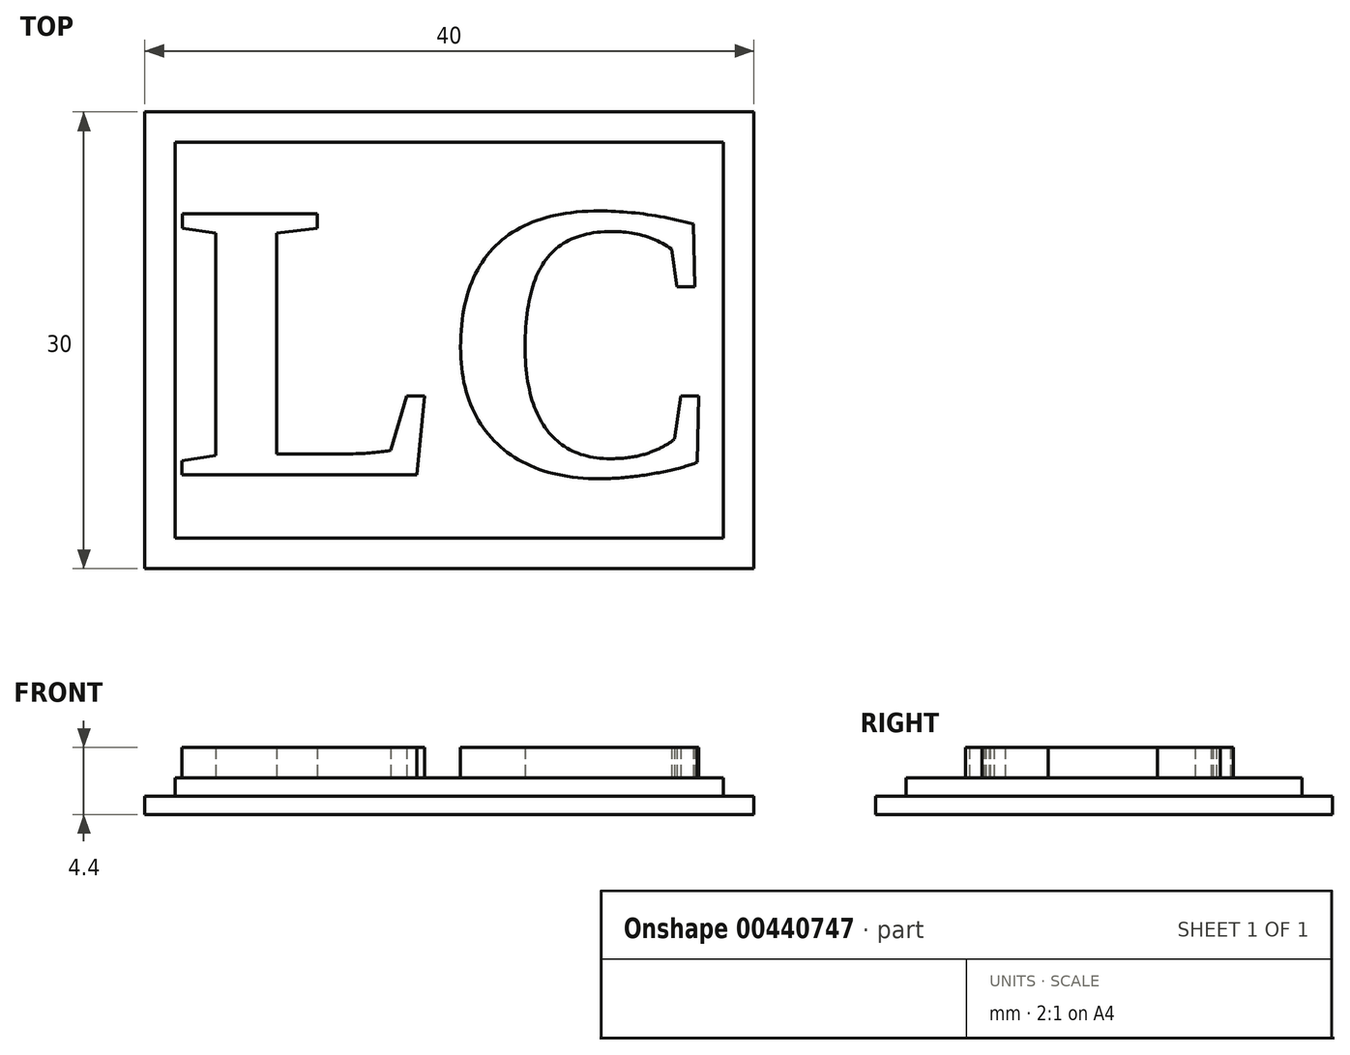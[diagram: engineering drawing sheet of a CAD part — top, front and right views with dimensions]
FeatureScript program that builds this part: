
annotation { "Feature Type Name" : "Feature", "Feature Type Description" : "" }
export const myFeature = defineFeature(function(context is Context, id is Id, definition is map)
    precondition{}
    {
        {
            var Q0;
            Q0=qCreatedBy(makeId("Top.planeOp"),FACE);
            var sketch = newSketch(context, id + "F0", { "sketchPlane" : qUnion([Q0])});
            skLineSegment(sketch, "E0.bottom", {"start": v(0, 0) * mm, "end": v(40, 0) * mm});
            skLineSegment(sketch, "E0.top", {"start": v(0, 30) * mm, "end": v(40, 30) * mm});
            skLineSegment(sketch, "E0.left", {"start": v(0, 0) * mm, "end": v(0, 30) * mm});
            skLineSegment(sketch, "E0.right", {"start": v(40, 0) * mm, "end": v(40, 30) * mm});
            skSolve(sketch);
        }
        {
            var Q0;
            Q0=qSketchRegion(id+"F0",true);
            extrude(context, id + "F1", {"entities" : qUnion([Q0]), "depth" : 1.2 * mm});
        }
        {
            var Q0;
            Q0=makeQuery(id+"F1.opExtrude","CAP_FACE",FACE,{"disambiguationData":[OSD([sQuery(id+"F0.wireOp",EDGE,"E0.bottom"),sQuery(id+"F0.wireOp",EDGE,"E0.top"),sQuery(id+"F0.wireOp",EDGE,"E0.left"),sQuery(id+"F0.wireOp",EDGE,"E0.right")])],"isStart":false});
            var sketch = newSketch(context, id + "F2", { "sketchPlane" : qUnion([Q0])});
            skLineSegment(sketch, "E1.0", {"start": v(38, 28) * mm, "end": v(2, 28) * mm});
            skLineSegment(sketch, "E1.1", {"start": v(38, 2) * mm, "end": v(38, 28) * mm});
            skLineSegment(sketch, "E1.2", {"start": v(2, 2) * mm, "end": v(38, 2) * mm});
            skLineSegment(sketch, "E1.3", {"start": v(2, 28) * mm, "end": v(2, 2) * mm});
            skSolve(sketch);
        }
        {
            var Q0;
            Q0=makeQuery(id+"F2.imprint","IMPRINT",FACE,{"disambiguationData":[TD([[makeQuery(id+"F2.imprint","IMPRINT",EDGE,{"derivedFrom":sQuery(id+"F2.wireOp",EDGE,"E1.0")}),1.0]])]});
            extrude(context, id + "F3", {"entities" : qUnion([Q0]), "operationType" : NewBodyOperationType.ADD, "depth" : 1.2 * mm});
        }
        {
            var Q0;
            Q0=makeQuery(id+"F3.opExtrude","CAP_FACE",FACE,{"disambiguationData":[OSD([sQuery(id+"F2.wireOp",EDGE,"E1.0"),sQuery(id+"F2.wireOp",EDGE,"E1.1"),sQuery(id+"F2.wireOp",EDGE,"E1.2"),sQuery(id+"F2.wireOp",EDGE,"E1.3")])],"isStart":false});
            var sketch = newSketch(context, id + "F4", { "sketchPlane" : qUnion([Q0])});
            skText(sketch, "E2", { "text": "LC", "fontName": "Tinos-Bold.ttf"});
            const initialGuessF4  = {"E2": [0.002, 0.00616, 1, 0, 0.01884]};
            skSetInitialGuess(sketch, initialGuessF4);
            skSolve(sketch);
        }
        {
            var Q0;
            Q0=qSketchRegion(id+"F4",true);
            extrude(context, id + "F5", {"entities" : qUnion([Q0]), "operationType" : NewBodyOperationType.ADD, "depth" : 2 * mm});
        }
    });
